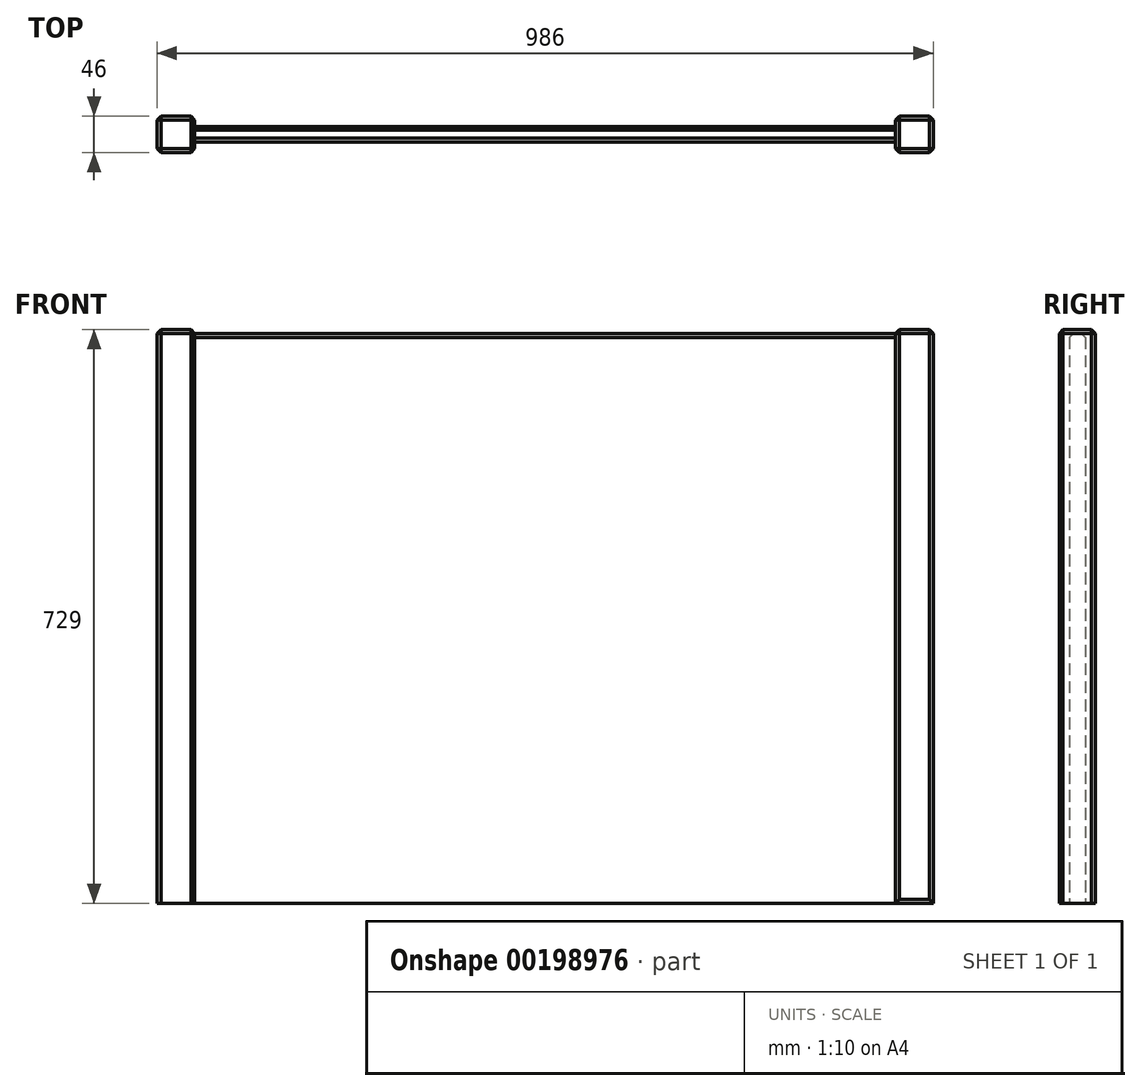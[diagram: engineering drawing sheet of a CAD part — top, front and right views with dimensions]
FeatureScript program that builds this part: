
annotation { "Feature Type Name" : "Feature", "Feature Type Description" : "" }
export const myFeature = defineFeature(function(context is Context, id is Id, definition is map)
    precondition{}
    {
        {
            var Q0;
            Q0=qCreatedBy(makeId("Front.planeOp"),FACE);
            var sketch = newSketch(context, id + "F0", { "sketchPlane" : qUnion([Q0])});
            skLineSegment(sketch, "E0.bottom", {"start": v(-439.83, 360.71) * mm, "end": v(450.17, 360.71) * mm});
            skLineSegment(sketch, "E0.top", {"start": v(-439.83, -363.29) * mm, "end": v(450.17, -363.29) * mm});
            skLineSegment(sketch, "E0.left", {"start": v(-439.83, 360.71) * mm, "end": v(-439.83, -363.29) * mm});
            skLineSegment(sketch, "E0.right", {"start": v(450.17, 360.71) * mm, "end": v(450.17, -363.29) * mm});
            skSolve(sketch);
        }
        {
            var Q0;
            Q0=makeQuery(id+"F0.imprint","IMPRINT",FACE,{"disambiguationData":[TD([[makeQuery(id+"F0.imprint","IMPRINT",EDGE,{"derivedFrom":sQuery(id+"F0.wireOp",EDGE,"E0.bottom")}),-1.0]])]});
            extrude(context, id + "F1", {"entities" : qUnion([Q0]), "depth" : 20 * mm});
        }
        {
            var Q0;
            Q0=makeQuery(id+"F1.opExtrude","SWEPT_FACE",FACE,{"disambiguationData":[OSD([sQuery(id+"F0.wireOp",EDGE,"E0.left")])]});
            var sketch = newSketch(context, id + "F2", { "sketchPlane" : qUnion([Q0])});
            skLineSegment(sketch, "E1.bottom", {"start": v(-13, 365.71) * mm, "end": v(33, 365.71) * mm});
            skLineSegment(sketch, "E1.top", {"start": v(-13, -363.29) * mm, "end": v(33, -363.29) * mm});
            skLineSegment(sketch, "E1.left", {"start": v(-13, 365.71) * mm, "end": v(-13, -363.29) * mm});
            skLineSegment(sketch, "E1.right", {"start": v(33, 365.71) * mm, "end": v(33, -363.29) * mm});
            skSolve(sketch);
        }
        {
            var Q0;
            Q0=makeQuery(id+"F2.imprint","IMPRINT",FACE,{"disambiguationData":[TD([[makeQuery(id+"F2.imprint","IMPRINT",EDGE,{"derivedFrom":sQuery(id+"F2.wireOp",EDGE,"E1.bottom")}),-1.0]])]});
            var Q1;
            {var subQ1=sQuery(id+"F0.wireOp",EDGE,"E0.left");var subQ2=makeQuery(id+"F1.opExtrude","CAP_EDGE",EDGE,{"disambiguationData":[OSD([subQ1])],"isStart":true});Q1=makeQuery(id+"F2.imprint","IMPRINT",FACE,{"disambiguationData":[TD([[makeQuery(id+"F2.imprint","IMPRINT",EDGE,{"derivedFrom":subQ2}),1.0]])]});}
            extrude(context, id + "F3", {"entities" : qUnion([Q0, Q1]), "operationType" : NewBodyOperationType.ADD, "depth" : 48 * mm});
        }
        {
            var Q0;
            Q0=makeQuery(id+"F1.opExtrude","SWEPT_FACE",FACE,{"disambiguationData":[OSD([sQuery(id+"F0.wireOp",EDGE,"E0.right")])]});
            var sketch = newSketch(context, id + "F4", { "sketchPlane" : qUnion([Q0])});
            skLineSegment(sketch, "E2.bottom", {"start": v(-33, 365.71) * mm, "end": v(13, 365.71) * mm});
            skLineSegment(sketch, "E2.top", {"start": v(-33, -363.29) * mm, "end": v(13, -363.29) * mm});
            skLineSegment(sketch, "E2.left", {"start": v(-33, 365.71) * mm, "end": v(-33, -363.29) * mm});
            skLineSegment(sketch, "E2.right", {"start": v(13, 365.71) * mm, "end": v(13, -363.29) * mm});
            skSolve(sketch);
        }
        {
            var Q0;
            {var subQ1=sQuery(id+"F0.wireOp",EDGE,"E0.right");var subQ2=makeQuery(id+"F1.opExtrude","CAP_EDGE",EDGE,{"disambiguationData":[OSD([subQ1])],"isStart":true});Q0=makeQuery(id+"F4.imprint","IMPRINT",FACE,{"disambiguationData":[TD([[makeQuery(id+"F4.imprint","IMPRINT",EDGE,{"derivedFrom":subQ2}),-1.0]])]});}
            var Q1;
            Q1=makeQuery(id+"F4.imprint","IMPRINT",FACE,{"disambiguationData":[TD([[makeQuery(id+"F4.imprint","IMPRINT",EDGE,{"derivedFrom":sQuery(id+"F4.wireOp",EDGE,"E2.bottom")}),-1.0]])]});
            extrude(context, id + "F5", {"entities" : qUnion([Q0, Q1]), "operationType" : NewBodyOperationType.ADD, "depth" : 48 * mm});
        }
        {
            var Q0;
            Q0=makeQuery(id+"F3.opExtrude","SWEPT_EDGE",EDGE,{"disambiguationData":[OSD([sQuery(id+"F2.wireOp",EDGE,"E1.bottom"),sQuery(id+"F2.wireOp",EDGE,"E1.right")])]});
            var Q1;
            Q1=makeQuery(id+"F3.opExtrude","CAP_EDGE",EDGE,{"disambiguationData":[OSD([sQuery(id+"F2.wireOp",EDGE,"E1.bottom")])],"isStart":false});
            var Q2;
            Q2=makeQuery(id+"F3.opExtrude","CAP_EDGE",EDGE,{"disambiguationData":[OSD([sQuery(id+"F2.wireOp",EDGE,"E1.bottom")])],"isStart":true});
            var Q3;
            Q3=makeQuery(id+"F3.opExtrude","SWEPT_EDGE",EDGE,{"disambiguationData":[OSD([sQuery(id+"F2.wireOp",EDGE,"E1.bottom"),sQuery(id+"F2.wireOp",EDGE,"E1.left")])]});
            var Q4;
            Q4=makeQuery(id+"F1.opExtrude","CAP_EDGE",EDGE,{"disambiguationData":[OSD([sQuery(id+"F0.wireOp",EDGE,"E0.bottom")])],"isStart":false});
            var Q5;
            Q5=makeQuery(id+"F1.opExtrude","CAP_EDGE",EDGE,{"disambiguationData":[OSD([sQuery(id+"F0.wireOp",EDGE,"E0.bottom")])],"isStart":true});
            var Q6;
            Q6=makeQuery(id+"F5.opExtrude","SWEPT_EDGE",EDGE,{"disambiguationData":[OSD([sQuery(id+"F4.wireOp",EDGE,"E2.bottom"),sQuery(id+"F4.wireOp",EDGE,"E2.right")])]});
            var Q7;
            Q7=makeQuery(id+"F5.opExtrude","CAP_EDGE",EDGE,{"disambiguationData":[OSD([sQuery(id+"F4.wireOp",EDGE,"E2.bottom")])],"isStart":true});
            var Q8;
            Q8=makeQuery(id+"F5.opExtrude","SWEPT_EDGE",EDGE,{"disambiguationData":[OSD([sQuery(id+"F4.wireOp",EDGE,"E2.bottom"),sQuery(id+"F4.wireOp",EDGE,"E2.left")])]});
            var Q9;
            Q9=makeQuery(id+"F5.opExtrude","CAP_EDGE",EDGE,{"disambiguationData":[OSD([sQuery(id+"F4.wireOp",EDGE,"E2.bottom")])],"isStart":false});
            var Q10;
            Q10=makeQuery(id+"F3.opExtrude","CAP_EDGE",EDGE,{"disambiguationData":[OSD([sQuery(id+"F2.wireOp",EDGE,"E1.left")])],"isStart":false});
            var Q11;
            Q11=makeQuery(id+"F3.opExtrude","CAP_EDGE",EDGE,{"disambiguationData":[OSD([sQuery(id+"F2.wireOp",EDGE,"E1.left")])],"isStart":true});
            var Q12;
            Q12=makeQuery(id+"F3.opExtrude","CAP_EDGE",EDGE,{"disambiguationData":[OSD([sQuery(id+"F2.wireOp",EDGE,"E1.right")])],"isStart":false});
            var Q13;
            Q13=makeQuery(id+"F3.opExtrude","CAP_EDGE",EDGE,{"disambiguationData":[OSD([sQuery(id+"F2.wireOp",EDGE,"E1.right")])],"isStart":true});
            var Q14;
            Q14=makeQuery(id+"F5.opExtrude","CAP_EDGE",EDGE,{"disambiguationData":[OSD([sQuery(id+"F4.wireOp",EDGE,"E2.left")])],"isStart":true});
            var Q15;
            Q15=makeQuery(id+"F5.opExtrude","SWEPT_FACE",FACE,{"disambiguationData":[OSD([sQuery(id+"F4.wireOp",EDGE,"E2.left")])]});
            var Q16;
            Q16=makeQuery(id+"F5.opExtrude","CAP_EDGE",EDGE,{"disambiguationData":[OSD([sQuery(id+"F4.wireOp",EDGE,"E2.right")])],"isStart":true});
            var Q17;
            Q17=makeQuery(id+"F5.opExtrude","CAP_EDGE",EDGE,{"disambiguationData":[OSD([sQuery(id+"F4.wireOp",EDGE,"E2.right")])],"isStart":false});
            chamfer(context, id + "F6", {"entities" : qUnion([Q0, Q1, Q2, Q3, Q4, Q5, Q6, Q7, Q8, Q9, Q10, Q11, Q12, Q13, Q14, Q15, Q16, Q17]), "width" : 5 * mm, "tangentPropagation" : true});
        }
    });
